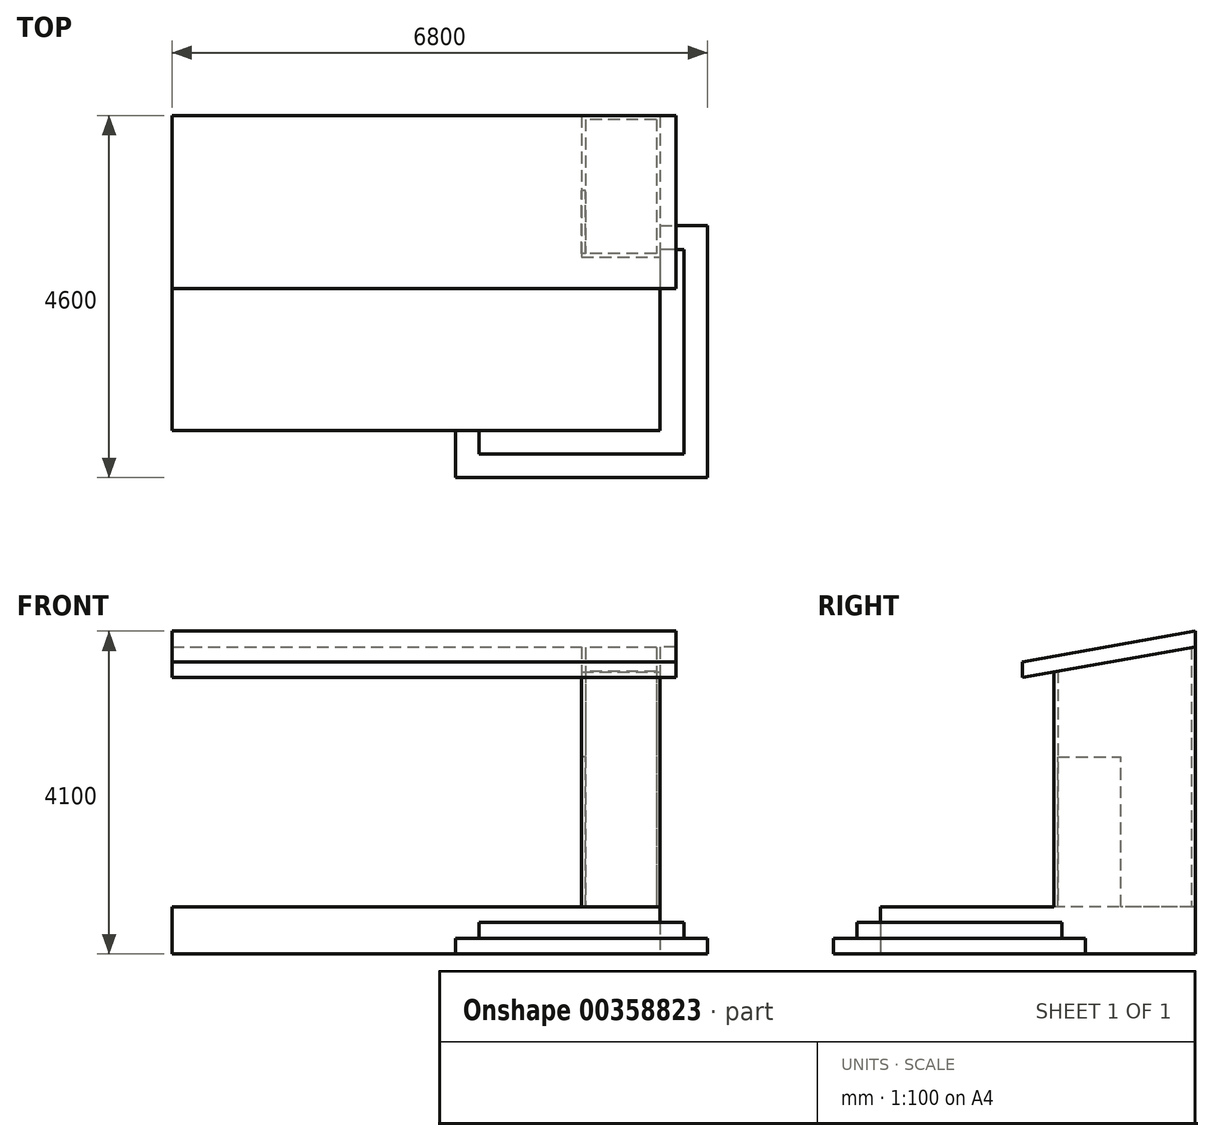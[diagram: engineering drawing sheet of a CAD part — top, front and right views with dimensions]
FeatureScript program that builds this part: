
annotation { "Feature Type Name" : "Feature", "Feature Type Description" : "" }
export const myFeature = defineFeature(function(context is Context, id is Id, definition is map)
    precondition{}
    {
        {
            var Q0;
            Q0=qCreatedBy(makeId("Top.planeOp"),FACE);
            var sketch = newSketch(context, id + "F0", { "sketchPlane" : qUnion([Q0])});
            skLineSegment(sketch, "E0.bottom", {"start": v(0, 0) * mm, "end": v(6200, 0) * mm});
            skLineSegment(sketch, "E0.top", {"start": v(0, -4000) * mm, "end": v(6200, -4000) * mm});
            skLineSegment(sketch, "E0.left", {"start": v(0, 0) * mm, "end": v(0, -4000) * mm});
            skLineSegment(sketch, "E0.right", {"start": v(6200, 0) * mm, "end": v(6200, -4000) * mm});
            skSolve(sketch);
        }
        {
            var Q0;
            Q0 = qSketchRegion(id + "F0", true);
            extrude(context, id + "F1", {"entities" : qUnion([Q0]), "depth" : 600 * mm});
        }
        {
            var Q0;
            Q0=makeQuery(id+"F1.opExtrude","CAP_FACE",FACE,{"disambiguationData":[OSD([sQuery(id+"F0.wireOp",EDGE,"E0.bottom"),sQuery(id+"F0.wireOp",EDGE,"E0.top"),sQuery(id+"F0.wireOp",EDGE,"E0.left"),sQuery(id+"F0.wireOp",EDGE,"E0.right")])],"isStart":true});
            var sketch = newSketch(context, id + "F2", { "sketchPlane" : qUnion([Q0])});
            skLineSegment(sketch, "E1.bottom", {"start": v(6200, 1400) * mm, "end": v(6800, 1400) * mm});
            skLineSegment(sketch, "E1.top", {"start": v(3600, 4600) * mm, "end": v(6800, 4600) * mm});
            skLineSegment(sketch, "E1.left", {"start": v(6200, 1400) * mm, "end": v(6200, 4000) * mm});
            skLineSegment(sketch, "E2.bottom", {"start": v(3600, 4000) * mm, "end": v(6200, 4000) * mm});
            skLineSegment(sketch, "E2.left", {"start": v(3600, 4000) * mm, "end": v(3600, 4600) * mm});
            skLineSegment(sketch, "E2.right", {"start": v(6800, 1400) * mm, "end": v(6800, 4600) * mm});
            skSolve(sketch);
        }
        {
            var Q0;
            Q0 = qSketchRegion(id + "F2", true);
            extrude(context, id + "F3", {"entities" : qUnion([Q0]), "operationType" : NewBodyOperationType.ADD, "oppositeDirection" : true, "depth" : 200 * mm});
        }
        {
            var Q0;
            Q0=makeQuery(id+"F3.opExtrude","CAP_FACE",FACE,{"disambiguationData":[OSD([sQuery(id+"F2.wireOp",EDGE,"E1.bottom"),sQuery(id+"F2.wireOp",EDGE,"E1.top"),sQuery(id+"F2.wireOp",EDGE,"E1.left"),sQuery(id+"F2.wireOp",EDGE,"E2.bottom"),sQuery(id+"F2.wireOp",EDGE,"E2.left"),sQuery(id+"F2.wireOp",EDGE,"E2.right")])],"isStart":false});
            var sketch = newSketch(context, id + "F4", { "sketchPlane" : qUnion([Q0])});
            skLineSegment(sketch, "E3.0", {"start": v(3900, -4300) * mm, "end": v(6500, -4300) * mm});
            skLineSegment(sketch, "E3.1", {"start": v(6500, -1700) * mm, "end": v(6500, -4300) * mm});
            skLineSegment(sketch, "E4.0", {"start": v(3900, -4000) * mm, "end": v(6200, -4000) * mm});
            skLineSegment(sketch, "E5.0", {"start": v(6200, -1700) * mm, "end": v(6200, -4000) * mm});
            skLineSegment(sketch, "E6", {"start": v(6500, -1700) * mm, "end": v(6200, -1700) * mm});
            skLineSegment(sketch, "E7", {"start": v(3900, -4300) * mm, "end": v(3900, -4000) * mm});
            skSolve(sketch);
        }
        {
            var Q0;
            Q0 = qSketchRegion(id + "F4", true);
            extrude(context, id + "F5", {"entities" : qUnion([Q0]), "operationType" : NewBodyOperationType.ADD, "depth" : 200 * mm});
        }
        {
            var Q0;
            Q0=makeQuery(id+"F1.opExtrude","CAP_FACE",FACE,{"disambiguationData":[OSD([sQuery(id+"F0.wireOp",EDGE,"E0.bottom"),sQuery(id+"F0.wireOp",EDGE,"E0.top"),sQuery(id+"F0.wireOp",EDGE,"E0.left"),sQuery(id+"F0.wireOp",EDGE,"E0.right")])],"isStart":false});
            var sketch = newSketch(context, id + "F6", { "sketchPlane" : qUnion([Q0])});
            skLineSegment(sketch, "E8.bottom", {"start": v(6200, 0) * mm, "end": v(5200, 0) * mm});
            skLineSegment(sketch, "E8.top", {"start": v(6200, -1800) * mm, "end": v(5200, -1800) * mm});
            skLineSegment(sketch, "E8.left", {"start": v(6200, 0) * mm, "end": v(6200, -1800) * mm});
            skLineSegment(sketch, "E8.right", {"start": v(5200, 0) * mm, "end": v(5200, -1800) * mm});
            skLineSegment(sketch, "E9.0", {"start": v(5250, -50) * mm, "end": v(5250, -1750) * mm});
            skLineSegment(sketch, "E9.1", {"start": v(6150, -50) * mm, "end": v(5250, -50) * mm});
            skLineSegment(sketch, "E9.2", {"start": v(6150, -50) * mm, "end": v(6150, -1750) * mm});
            skLineSegment(sketch, "E9.3", {"start": v(6150, -1750) * mm, "end": v(5250, -1750) * mm});
            skSolve(sketch);
        }
        {
            var Q0;
            Q0 = qSketchRegion(id + "F6", true);
            extrude(context, id + "F7", {"entities" : qUnion([Q0]), "operationType" : NewBodyOperationType.ADD, "depth" : 3300 * mm});
        }
        {
            var Q0;
            Q0=makeQuery(id+"F7.boolean.opBoolean","MERGE",FACE,{"derivedFrom":[makeQuery(id+"F1.opExtrude","SWEPT_FACE",FACE,{"disambiguationData":[OSD([sQuery(id+"F0.wireOp",EDGE,"E0.right")])]}),makeQuery(id+"F7.opExtrude","SWEPT_FACE",FACE,{"disambiguationData":[OSD([sQuery(id+"F6.wireOp",EDGE,"E8.left")])]})]});
            var sketch = newSketch(context, id + "F8", { "sketchPlane" : qUnion([Q0])});
            skLineSegment(sketch, "E10", {"start": v(0, 3900) * mm, "end": v(-1800, 3582.61) * mm});
            skLineSegment(sketch, "E11", {"start": v(-1800, 3582.61) * mm, "end": v(-1800, 3900) * mm});
            skLineSegment(sketch, "E12", {"start": v(-1800, 3900) * mm, "end": v(0, 3900) * mm});
            skSolve(sketch);
        }
        {
            var Q0;
            Q0 = qSketchRegion(id + "F8", true);
            extrude(context, id + "F9", {"entities" : qUnion([Q0]), "operationType" : NewBodyOperationType.REMOVE, "endBound" : BoundingType.THROUGH_ALL, "oppositeDirection" : true, "depth" : 25 * mm});
        }
        {
            var Q0;
            Q0=makeQuery(id+"F7.boolean.opBoolean","MERGE",FACE,{"derivedFrom":[makeQuery(id+"F1.opExtrude","SWEPT_FACE",FACE,{"disambiguationData":[OSD([sQuery(id+"F0.wireOp",EDGE,"E0.right")])]}),makeQuery(id+"F7.opExtrude","SWEPT_FACE",FACE,{"disambiguationData":[OSD([sQuery(id+"F6.wireOp",EDGE,"E8.left")])]})]});
            var sketch = newSketch(context, id + "F10", { "sketchPlane" : qUnion([Q0])});
            skLineSegment(sketch, "E13", {"start": v(0, 3900) * mm, "end": v(-2200, 3512.08) * mm});
            skLineSegment(sketch, "E14", {"start": v(-2200, 3512.08) * mm, "end": v(-2200, 3712.08) * mm});
            skLineSegment(sketch, "E15", {"start": v(-2200, 3712.08) * mm, "end": v(0, 4100) * mm});
            skLineSegment(sketch, "E16", {"start": v(0, 4100) * mm, "end": v(0, 3900) * mm});
            skSolve(sketch);
        }
        {
            var Q0;
            Q0 = qSketchRegion(id + "F10", true);
            extrude(context, id + "F11", {"entities" : qUnion([Q0]), "operationType" : NewBodyOperationType.ADD, "oppositeDirection" : true, "depth" : 6200 * mm});
        }
        {
            var Q0;
            Q0 = qSketchRegion(id + "F10", true);
            extrude(context, id + "F12", {"entities" : qUnion([Q0]), "operationType" : NewBodyOperationType.ADD, "depth" : 200 * mm});
        }
        {
            var Q0;
            Q0=makeQuery(id+"F7.opExtrude","SWEPT_FACE",FACE,{"disambiguationData":[OSD([sQuery(id+"F6.wireOp",EDGE,"E8.right")])]});
            var sketch = newSketch(context, id + "F13", { "sketchPlane" : qUnion([Q0])});
            skLineSegment(sketch, "E17.bottom", {"start": v(1750, 600) * mm, "end": v(950, 600) * mm});
            skLineSegment(sketch, "E17.top", {"start": v(1750, 2500) * mm, "end": v(950, 2500) * mm});
            skLineSegment(sketch, "E17.left", {"start": v(1750, 600) * mm, "end": v(1750, 2500) * mm});
            skLineSegment(sketch, "E17.right", {"start": v(950, 600) * mm, "end": v(950, 2500) * mm});
            skSolve(sketch);
        }
        {
            var Q0;
            Q0 = qSketchRegion(id + "F13", true);
            extrude(context, id + "F14", {"entities" : qUnion([Q0]), "operationType" : NewBodyOperationType.REMOVE, "endBound" : BoundingType.UP_TO_NEXT, "oppositeDirection" : true, "depth" : 25 * mm});
        }
    });
